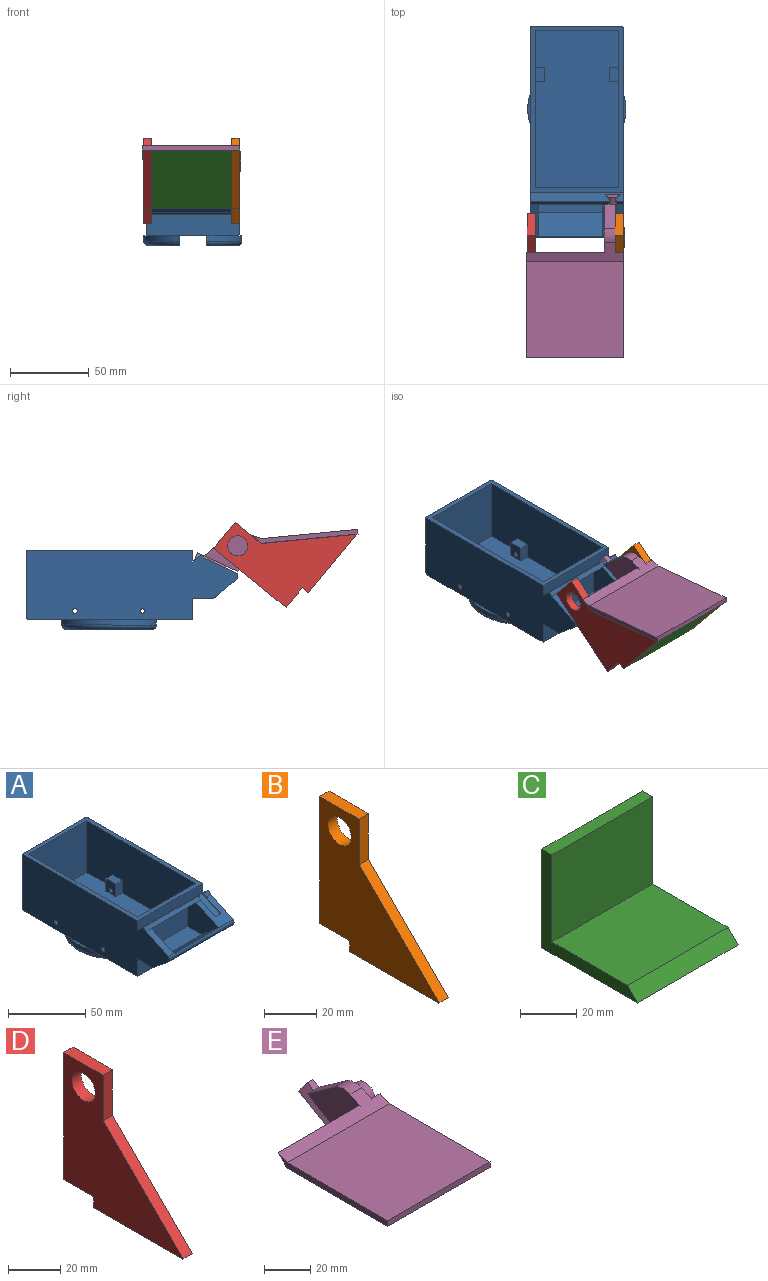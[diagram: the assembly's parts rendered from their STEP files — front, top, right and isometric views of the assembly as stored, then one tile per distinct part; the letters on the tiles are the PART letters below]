
ASSEMBLY  parts=5 mates=9
PART A: 61 faces, bbox 67.5x134.5x50.4 mm
  f0: plane 53.78x19.7mm, normal (0,0,1), area 777.1mm2, adj f1,f59
  f1: cylinder r=28.2mm len=53.78mm, axis (0,0,1), area 242.5mm2, adj f0,f15,f52,f59
  f2: cylinder r=31.2mm len=60.04mm, axis (0,0,1), area 274.7mm2, adj f3,f15,f52,f59
  f3: torus R=28.2mm, axis (0,0,1), area 364.5mm2, adj f2,f4,f59
  f4: plane 53.78x19.7mm, normal (0,0,-1), area 777.1mm2, adj f3,f59
  f5: plane 99.5x53.1mm, normal (0,0,1), area 5175.4mm2, adj f6,f16,f17,f18,f40,f41,f42,f44
  f6: plane 99.5x41mm, normal (1,0,0), area 3982.4mm2, adj f5,f17,f18,f22,f40,f41,f43,f49
  f7: plane 4.86x2.3mm, normal (0,-0.77,0.64), area 13.5mm2, adj f8,f9,f20,f30
  f8: plane 59.1x5.73mm, normal (0,0.64,0.77), area 406.4mm2, adj f7,f14,f20,f23,f26,f30,f31,f32
  f9: plane 20.66x13.4mm, normal (0,-0.42,0.91), area 228.1mm2, adj f7,f20,f26,f29,f30,f32,f33,f35
  f10: plane 40.7x15.98mm, normal (0,-1,0), area 650.5mm2, adj f11,f13,f28,f29
  f11: plane 40.7x13mm, normal (0,0,1), area 529.1mm2, adj f10,f12,f28,f29
  f12: plane 40.7x15.32mm, normal (0,0.64,0.77), area 814mm2, adj f11,f28,f29,f35
  f13: plane 40.7x7.66mm, normal (0,-0.64,-0.77), area 407mm2, adj f10,f26,f28,f29
  f14: plane 59.1x7.26mm, normal (0,-1,0), area 429.1mm2, adj f8,f20,f22,f23
  f15: plane 103.5x57.1mm, normal (0,0,-1), area 5542.5mm2, adj f1,f2,f19,f23,f36,f37,f54,f56
  f16: plane 99.5x41mm, normal (-1,0,0), area 3982.4mm2, adj f5,f17,f18,f22,f44,f45,f47,f51
  f17: plane 53.1x41mm, normal (0,-1,0), area 2177.1mm2, adj f5,f6,f16,f22
  f18: plane 53.1x41mm, normal (0,1,0), area 2177.1mm2, adj f5,f6,f16,f22
  f19: plane 59.1x13.84mm, normal (0,-1,0), area 817.1mm2, adj f15,f20,f23,f24,f36
  f20: plane 132.52x42mm, normal (1,0,0), area 4872.2mm2, adj f7,f8,f9,f14,f19,f22,f24,f25
  f21: plane 57.1x42mm, normal (0,1,0), area 2398.2mm2, adj f22,f23,f37,f39
  f22: plane 105.5x59.1mm, normal (0,0,1), area 950.7mm2, adj f6,f14,f16,f17,f18,f20,f21,f23
  f23: plane 134.52x44mm, normal (-1,0,0), area 5166.3mm2, adj f8,f14,f15,f19,f21,f22,f24,f25
  f24: plane 59.1x13mm, normal (0,0,-1), area 768.3mm2, adj f19,f20,f23,f34
  f25: plane 59.1x13.02mm, normal (0,-0.64,-0.77), area 1004.7mm2, adj f20,f23,f34,f35
  f26: plane 50.56x2.3mm, normal (0,-0.77,0.64), area 150.6mm2, adj f8,f9,f13,f23,f27,f32
  f27: plane 20.66x9.56mm, normal (0,-0.42,0.91), area 113.8mm2, adj f23,f26,f28,f35
  f28: plane 28.32x22.41mm, normal (1,0,0), area 412.9mm2, adj f10,f11,f12,f13,f27
  f29: plane 28.32x22.41mm, normal (-1,0,0), area 412.9mm2, adj f9,f10,f11,f12,f13
  f30: plane 19.7x11.92mm, normal (-0.87,0.21,-0.45), area 83.9mm2, adj f7,f8,f9,f31,f33
  f31: plane 18.15x9.4mm, normal (0,-0.42,0.91), area 188mm2, adj f8,f30,f32,f33
  f32: plane 19.7x11.92mm, normal (0.87,0.21,-0.45), area 83.9mm2, adj f8,f9,f26,f31,f33
  f33: plane 9.4x3.35mm, normal (0,0.91,0.42), area 26.8mm2, adj f9,f30,f31,f32
  f34: cylinder r=3mm len=59.1mm, axis (-1,0,0), area 123.8mm2, adj f20,f23,f24,f25
  f35: cylinder r=3mm len=59.1mm, axis (-1,0,0), area 278.5mm2, adj f9,f12,f20,f23,f25,f27
  f36: cylinder r=2mm len=103.5mm, axis (0,1,0), area 325.2mm2, adj f15,f19,f20,f38,f52
  f37: cylinder r=2mm len=57.1mm, axis (-1,0,0), area 179.4mm2, adj f15,f21,f23,f38
  f38: sphere r=2mm, area 6.3mm2, adj f36,f37,f39
  f39: cylinder r=2mm len=42mm, axis (0,0,-1), area 131.9mm2, adj f20,f21,f22,f38
  f40: plane 10x6mm, normal (0,1,0), area 60mm2, adj f5,f6,f42,f43
  f41: plane 10x6mm, normal (0,-1,0), area 60mm2, adj f5,f6,f42,f43
  f42: plane 10x9mm, normal (1,0,0), area 82.9mm2, adj f5,f40,f41,f43,f48
  f43: plane 9x6mm, normal (0,0,1), area 54mm2, adj f6,f40,f41,f42
  f44: plane 10x6mm, normal (0,-1,0), area 60mm2, adj f5,f16,f46,f47
  f45: plane 10x6mm, normal (0,1,0), area 60mm2, adj f5,f16,f46,f47
  f46: plane 10x9mm, normal (-1,0,0), area 82.9mm2, adj f5,f44,f45,f47,f50
  f47: plane 9x6mm, normal (0,0,1), area 54mm2, adj f16,f44,f45,f46
  f48: cylinder r=1.5mm len=9mm, axis (-1,0,0), area 84.8mm2, adj f23,f42
  f49: cylinder r=1.5mm len=3mm, axis (-1,0,0), area 28.3mm2, adj f6,f23
  f50: cylinder r=1.5mm len=9mm, axis (1,0,0), area 84.8mm2, adj f20,f46
  f51: cylinder r=1.5mm len=3mm, axis (1,0,0), area 28.3mm2, adj f16,f20
  f52: plane 29.29x3.65mm, normal (0,0,1), area 66.9mm2, adj f1,f2,f36
  f53: plane 53.78x19.7mm, normal (0,0,1), area 777.1mm2, adj f54,f60
  f54: cylinder r=28.2mm len=53.78mm, axis (0,0,1), area 242.5mm2, adj f15,f53,f60
  f55: plane 20.02x1.65mm, normal (0,0,1), area 22.1mm2, adj f23,f56
  f56: cylinder r=31.2mm len=60.04mm, axis (0,0,1), area 274.7mm2, adj f15,f55,f57,f60
  f57: torus R=28.2mm, axis (0,0,1), area 364.5mm2, adj f56,f58,f60
  f58: plane 53.78x19.7mm, normal (0,0,-1), area 777.1mm2, adj f57,f60
  f59: plane 60.04x6.4mm, normal (-1,0,0), area 197.4mm2, adj f0,f1,f2,f3,f4,f15
  f60: plane 60.04x6.4mm, normal (1,0,0), area 197.4mm2, adj f15,f53,f54,f56,f57,f58
PART B: 10 faces, bbox 5.1x64.5x64.5 mm
  f0: plane 16.25x5.08mm, normal (0,0,-1), area 82.5mm2, adj f3,f6,f7,f8
  f1: plane 21.33x5.08mm, normal (0,-1,0), area 108.3mm2, adj f2,f5,f6,f7
  f2: plane 21.33x5.08mm, normal (0,0,1), area 108.3mm2, adj f1,f3,f6,f7
  f3: plane 59.43x5.08mm, normal (0,1,0), area 301.9mm2, adj f0,f2,f6,f7
  f4: cylinder r=6.35mm len=12.7mm, axis (1,0,0), area 202.7mm2, adj f6,f7
  f5: plane 43.18x43.18mm, normal (0,-0.71,0.71), area 310.2mm2, adj f1,f6,f7,f9
  f6: plane 64.51x64.51mm, normal (-1,0,0), area 2098.7mm2, adj f0,f1,f2,f3,f4,f5,f8,f9
  f7: plane 64.51x64.51mm, normal (1,0,0), area 2098.7mm2, adj f0,f1,f2,f3,f4,f5,f8,f9
  f8: plane 5.08x5.08mm, normal (0,1,0), area 25.8mm2, adj f0,f6,f7,f9
  f9: plane 48.26x5.08mm, normal (0,0,-1), area 245.2mm2, adj f5,f6,f7,f8
PART C: 8 faces, bbox 50.8x48.3x43.2 mm
  f0: plane 50.8x38.1mm, normal (0,0,1), area 1935.5mm2, adj f1,f5,f6,f7
  f1: plane 50.8x5.08mm, normal (0,-0.71,0.71), area 365mm2, adj f0,f2,f6,f7
  f2: plane 50.8x48.26mm, normal (0,0,-1), area 2451.6mm2, adj f1,f3,f6,f7
  f3: plane 50.8x43.18mm, normal (0,1,0), area 2193.5mm2, adj f2,f4,f6,f7
  f4: plane 50.8x5.08mm, normal (0,0,1), area 258.1mm2, adj f3,f5,f6,f7
  f5: plane 50.8x38.1mm, normal (0,-1,0), area 1935.5mm2, adj f0,f4,f6,f7
  f6: plane 48.26x43.18mm, normal (1,0,0), area 425.8mm2, adj f0,f1,f2,f3,f4,f5
  f7: plane 48.26x43.18mm, normal (-1,0,0), area 425.8mm2, adj f0,f1,f2,f3,f4,f5
PART D: 10 faces, bbox 5.1x64.5x64.5 mm
  f0: plane 16.25x5.08mm, normal (0,0,-1), area 82.5mm2, adj f3,f6,f7,f8
  f1: plane 21.33x5.08mm, normal (0,-1,0), area 108.3mm2, adj f2,f5,f6,f7
  f2: plane 21.33x5.08mm, normal (0,0,1), area 108.3mm2, adj f1,f3,f6,f7
  f3: plane 59.43x5.08mm, normal (0,1,0), area 301.9mm2, adj f0,f2,f6,f7
  f4: cylinder r=6.35mm len=12.7mm, axis (1,0,0), area 202.7mm2, adj f6,f7
  f5: plane 43.18x43.18mm, normal (0,-0.71,0.71), area 310.2mm2, adj f1,f6,f7,f9
  f6: plane 64.51x64.51mm, normal (-1,0,0), area 2098.7mm2, adj f0,f1,f2,f3,f4,f5,f8,f9
  f7: plane 64.51x64.51mm, normal (1,0,0), area 2098.7mm2, adj f0,f1,f2,f3,f4,f5,f8,f9
  f8: plane 5.08x5.08mm, normal (0,1,0), area 25.8mm2, adj f0,f6,f7,f9
  f9: plane 48.26x5.08mm, normal (0,0,-1), area 245.2mm2, adj f5,f6,f7,f8
PART E: 22 faces, bbox 62.9x104.9x25.7 mm
  f0: plane 17.24x10.14mm, normal (0,0.51,-0.86), area 180mm2, adj f1,f3,f4,f5
  f1: plane 19.76x14.41mm, normal (0.87,-0.25,0.43), area 114.6mm2, adj f0,f2,f4,f5,f12
  f2: plane 3.74x3.27mm, normal (0,-0.51,0.86), area 14.2mm2, adj f1,f3,f5,f9
  f3: plane 19.76x14.41mm, normal (-0.87,-0.25,0.43), area 114.6mm2, adj f0,f2,f4,f5,f6
  f4: plane 9x4.28mm, normal (0,-0.86,-0.51), area 30.4mm2, adj f0,f1,f3,f6
  f5: plane 9x4.28mm, normal (0,0.86,0.51), area 30.4mm2, adj f0,f1,f2,f3
  f6: plane 20.24x11.9mm, normal (0,0.51,-0.86), area 113.1mm2, adj f3,f4,f9,f10,f11,f12
  f7: plane 62.08x11.57mm, normal (0,-0.42,0.91), area 424.7mm2, adj f8,f11,f12,f13,f14,f17,f18,f19
  f8: cylinder r=9.25mm len=9.23mm, axis (1,0,0), area 68mm2, adj f7,f9,f11,f12
  f9: plane 16.54x11.8mm, normal (0,0.58,0.81), area 142.2mm2, adj f2,f6,f8,f11,f12
  f10: plane 17.09x16.27mm, normal (0,-0.69,-0.72), area 165.2mm2, adj f6,f11,f12,f15
  f11: plane 37.33x25.42mm, normal (-1,0,0), area 510.7mm2, adj f6,f7,f8,f9,f10,f14
  f12: plane 37.33x25.42mm, normal (1,0,0), area 387.9mm2, adj f1,f6,f7,f8,f9,f10,f13,f20
  f13: plane 5.54x5.54mm, normal (0,0.71,-0.71), area 41.4mm2, adj f7,f12,f15,f18
  f14: plane 49.8x5.54mm, normal (0,0.71,-0.71), area 390.1mm2, adj f7,f11,f15,f19
  f15: plane 62.08x61.37mm, normal (0,0,-1), area 3809.6mm2, adj f10,f13,f14,f16,f18,f19
  f16: plane 62.08x3mm, normal (0,-1,0), area 186.2mm2, adj f15,f17,f18,f19
  f17: plane 62.08x61.37mm, normal (0,0,1), area 3809.6mm2, adj f7,f16,f18,f19
  f18: plane 66.91x5.54mm, normal (1,0,0), area 192.4mm2, adj f7,f13,f15,f16,f17
  f19: plane 66.91x5.54mm, normal (-1,0,0), area 192.4mm2, adj f7,f14,f15,f16,f17
  f20: cylinder r=6.25mm len=12.5mm, axis (-1,0,0), area 238.8mm2, adj f12,f21
  f21: plane 12.5x12.5mm, normal (1,0,0), area 122.7mm2, adj f20
PLACE A rot(axis=(1,0,0),0.1deg) t=(-40.51,193.65,58.17)mm
PLACE B rot(axis=(-1,0,0),50.5deg) t=(-75.92,136.62,34.08)mm
PLACE C rot(axis=(-1,0,0),50.5deg) t=(-75.92,136.62,34.08)mm
PLACE D rot(axis=(-1,0,0),50.5deg) t=(-75.92,136.62,34.08)mm
PLACE E rot(axis=(-1,0,0),5.5deg) t=(-17.66,189.03,96.18)mm
MATE parallel D.f7 <-> B.f6  axis (1,0,0) through (-66.83,131.75,94.99)mm
MATE slider E.f4 <-> A.f33  axis (0,-0.91,-0.42) through (-17.66,170.9,87.75)mm
MATE planar C.f6 <-> B.f6  axis (1,0,0) through (-16.03,101.32,93.87)mm
MATE planar B.f4 <-> E.f8  axis (-1,0,0) through (-16.03,161.61,105.21)mm
MATE fastened B.f6 <-> C.f6  axis (-1,0,0) through (-16.03,101.32,93.87)mm
MATE cylindrical B.f4 <-> E.f8  axis (1,0,0) through (-10.95,161.61,105.21)mm
MATE planar E.f4 <-> A.f33  axis (0,-0.91,-0.42) through (-17.66,170.9,87.75)mm
MATE planar C.f7 <-> D.f7  axis (-1,0,0) through (-66.83,101.32,93.87)mm
MATE fastened C.f7 <-> D.f7  axis (-1,0,0) through (-66.83,101.32,93.87)mm
